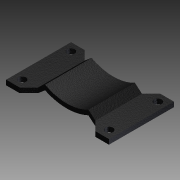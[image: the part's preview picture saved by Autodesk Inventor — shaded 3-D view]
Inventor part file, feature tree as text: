
AUTODESK INVENTOR PART (.ipt)
format: ipt  version: 2012 (Build 160160000, 160)  size: 158,208 bytes
history: native  units: in
note: dims shown in document units (in); Inventor stores cm internally (conversion verified against a paired STEP export)
features: sketch x3, projected_geometry x3, extrude x2, hole x1, mirror x1
ambient origin geometry x8: Origin, YZ Plane, XZ Plane, XY Plane, X Axis, Y Axis, Z Axis, Center Point
bodies: Solid1 (feature_tree)
feature tree (10):
  extrude  "Extrusion1"  Depth=0.625in
  extrude  "Extrusion2"  TaperAngle=45.0deg  [1 undecoded]
  hole  "Hole1"  [1 undecoded]
  mirror  "Mirror1"
  sketch  "Sketch1"  dims[d1=3.0in d2=0.625in]
  sketch  "Sketch2"  dims[d3=2.15in d4=45.0deg]
  projected_geometry  "Projected Loop1"
  projected_geometry  "Projected Loop2"
  projected_geometry  "Projected Loop3"
  sketch  "Sketch3"  dims[d5=2.15in d6=4.75in d7=0.625in d8=45.0deg d9=0.425in d10=0.5in d11=0.0in d12=2.0in d13=2.125in d14=0.2in d15=0.125in d17=0.125in d18=0.5in d19=0.0in d20=2.25in d21=0.365in d22=0.35in d23=0.75in d24=0.375in d25=0.25in d26=0.5635in d27=1.0in d28=0.8108in]
note: 2 required parameter values undecoded (feature->parameter linkage not recoverable at this tier; creation-order binding heuristic only, values carry confidence <= 0.55)
